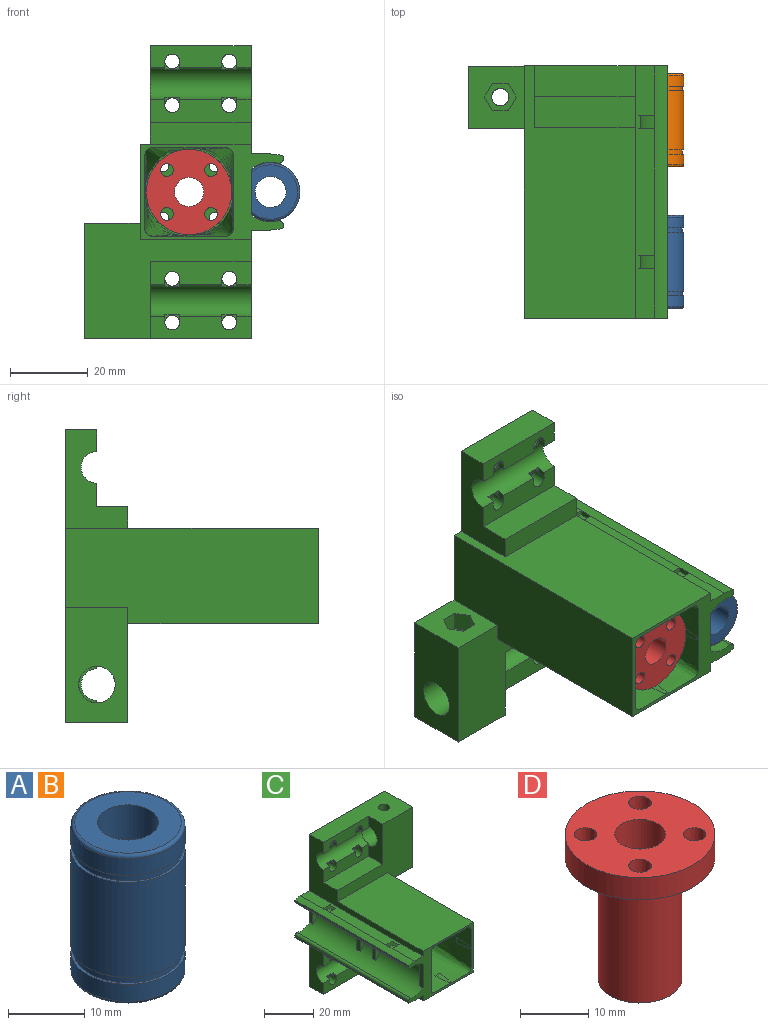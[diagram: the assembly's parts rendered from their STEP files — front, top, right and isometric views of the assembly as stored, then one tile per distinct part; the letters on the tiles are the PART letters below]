
ASSEMBLY  parts=4 mates=1
PART A: 14 faces, bbox 16.2x16.2x24 mm
  f0: plane 15x15mm, normal (0,0,-1), area 16.1mm2, adj f1,f10
  f1: cylinder r=7.15mm len=14.3mm, axis (0,0,-1), area 49.4mm2, adj f0,f2
  f2: plane 15x15mm, normal (0,0,1), area 16.1mm2, adj f1,f3
  f3: cylinder r=7.5mm len=15mm, axis (0,0,-1), area 129.6mm2, adj f2,f12
  f4: plane 14x14mm, normal (0,0,-1), area 103.7mm2, adj f11,f12
  f5: plane 14x14mm, normal (0,0,1), area 103.7mm2, adj f11,f13
  f6: cylinder r=7.5mm len=15mm, axis (0,0,-1), area 129.6mm2, adj f7,f13
  f7: plane 15x15mm, normal (0,0,-1), area 16.1mm2, adj f6,f8
  f8: cylinder r=7.15mm len=14.3mm, axis (0,0,-1), area 49.4mm2, adj f7,f9
  f9: plane 15x15mm, normal (0,0,1), area 16.1mm2, adj f8,f10
  f10: cylinder r=7.5mm len=15.3mm, axis (0,0,-1), area 721mm2, adj f0,f9
  f11: cylinder r=4mm len=24mm, axis (0,0,1), area 603.2mm2, adj f4,f5
  f12: torus R=7mm, axis (0,0,1), area 36.1mm2, adj f3,f4
  f13: torus R=7mm, axis (0,0,-1), area 36.1mm2, adj f5,f6
PART B: same geometry as A
PART C: 212 faces, bbox 51.5x65.2x75.5 mm
  f0: cylinder r=1.58mm len=4mm, axis (0,1,0), area 39.7mm2, adj f195,f203
  f1: cylinder r=1.58mm len=4mm, axis (0,1,0), area 39.7mm2, adj f188,f203
  f2: cylinder r=1.58mm len=4mm, axis (0,1,0), area 39.7mm2, adj f181,f203
  f3: cylinder r=1.58mm len=4mm, axis (0,1,0), area 39.7mm2, adj f174,f203
  f4: cylinder r=6.44mm len=16mm, axis (0,-1,0), area 647.2mm2, adj f43,f203
  f5: plane 65x5mm, normal (0,0,1), area 299.9mm2, adj f6,f8,f12,f15,f17,f21,f27,f28
  f6: cylinder r=10.43mm len=4.14mm, axis (0,-1,0), area 17.7mm2, adj f5,f8,f12,f173
  f7: cylinder r=10.43mm len=4.14mm, axis (0,-1,0), area 17.7mm2, adj f9,f13,f30,f172
  f8: plane 7.73x6.42mm, normal (0,1,0), area 16.7mm2, adj f5,f6,f10,f148,f173
  f9: plane 7.73x6.42mm, normal (0,1,0), area 16.7mm2, adj f7,f11,f30,f149,f172
  f10: cylinder r=8.43mm len=7.73mm, axis (0,-1,0), area 34.2mm2, adj f8,f12,f148,f173
  f11: cylinder r=8.43mm len=7.73mm, axis (0,-1,0), area 34.2mm2, adj f9,f13,f149,f172
  f12: plane 7.73x6.42mm, normal (0,-1,0), area 16.7mm2, adj f5,f6,f10,f148,f173
  f13: plane 7.73x6.42mm, normal (0,-1,0), area 16.7mm2, adj f7,f11,f30,f149,f172
  f14: cylinder r=10.43mm len=4.14mm, axis (0,1,0), area 17.7mm2, adj f16,f20,f30,f171
  f15: cylinder r=10.43mm len=4.14mm, axis (0,1,0), area 17.7mm2, adj f5,f17,f21,f170
  f16: plane 7.73x6.42mm, normal (0,-1,0), area 16.7mm2, adj f14,f18,f30,f151,f171
  f17: plane 7.73x6.42mm, normal (0,-1,0), area 16.7mm2, adj f5,f15,f19,f150,f170
  f18: cylinder r=8.43mm len=7.73mm, axis (0,1,0), area 34.2mm2, adj f16,f20,f151,f171
  f19: cylinder r=8.43mm len=7.73mm, axis (0,1,0), area 34.2mm2, adj f17,f21,f150,f170
  f20: plane 7.73x6.42mm, normal (0,1,0), area 16.7mm2, adj f14,f18,f30,f151,f171
  f21: plane 7.73x6.42mm, normal (0,1,0), area 16.7mm2, adj f5,f15,f19,f150,f170
  f22: cylinder r=2.24mm len=5.52mm, axis (0,0,-1), area 73.7mm2, adj f76,f166
  f23: plane 19.8x8mm, normal (-1,0,0), area 123.7mm2, adj f32,f37,f76,f108,f109,f166
  f24: cylinder r=2.24mm len=11.03mm, axis (0,0,-1), area 151.4mm2, adj f158,f166
  f25: plane 25.32x16mm, normal (1,0,0), area 220.3mm2, adj f31,f35,f39,f43,f44,f106,f107,f169
  f26: cylinder r=7.73mm len=65mm, axis (0,1,0), area 1734mm2, adj f27,f43,f138,f139,f140,f141,f142,f143
  f27: plane 37.08x24.87mm, normal (0,-1,0), area 9.6mm2, adj f5,f26,f28,f29,f30,f40,f77,f147
  f28: cylinder r=9.79mm len=65mm, axis (0,1,0), area 216.3mm2, adj f5,f27,f43,f148,f150,f153
  f29: cylinder r=9.79mm len=65mm, axis (0,1,0), area 216.3mm2, adj f27,f30,f43,f149,f151,f152
  f30: plane 65x5mm, normal (0,0,-1), area 299.9mm2, adj f7,f9,f13,f14,f16,f20,f27,f29
  f31: plane 26x5.55mm, normal (0,-1,0), area 121.3mm2, adj f25,f39,f40,f44,f60,f68,f111,f112
  f32: plane 26x6.05mm, normal (0,-1,0), area 134.2mm2, adj f23,f33,f38,f41,f77,f109,f125,f126
  f33: cylinder r=1.9mm len=4.1mm, axis (0,1,0), area 37.6mm2, adj f32,f84,f130,f131,f133
  f34: cylinder r=1.9mm len=4.1mm, axis (0,1,0), area 37mm2, adj f37,f98,f127,f128,f129
  f35: plane 26x6.05mm, normal (0,-1,0), area 134.2mm2, adj f25,f36,f39,f40,f52,f107,f114,f115
  f36: cylinder r=1.9mm len=4.1mm, axis (0,1,0), area 37mm2, adj f35,f51,f121,f122,f123
  f37: plane 26x5.55mm, normal (0,-1,0), area 121.3mm2, adj f23,f34,f38,f42,f76,f77,f128,f129
  f38: cylinder r=4.1mm len=26mm, axis (-1,0,0), area 303.2mm2, adj f32,f37,f77,f124,f125,f126,f127,f128
  f39: cylinder r=4.1mm len=26mm, axis (-1,0,0), area 303.2mm2, adj f25,f31,f35,f40,f110,f111,f112,f114
  f40: plane 65x27.86mm, normal (-1,0,0), area 385.2mm2, adj f27,f30,f31,f35,f39,f43,f44,f106
  f41: cylinder r=1.9mm len=4.1mm, axis (0,1,0), area 37mm2, adj f32,f91,f124,f125,f126
  f42: cylinder r=1.9mm len=4.1mm, axis (0,1,0), area 37.6mm2, adj f37,f105,f134,f136,f137
  f43: plane 75.3x51.25mm, normal (0,1,0), area 2052.3mm2, adj f4,f5,f25,f26,f28,f29,f30,f40
  f44: plane 26x8mm, normal (0,0,-1), area 208mm2, adj f25,f31,f40,f43
  f45: plane 3.9x3.08mm, normal (-0.87,0,0.5), area 13.9mm2, adj f43,f46,f50,f51
  f46: plane 3.9x3.08mm, normal (-0.87,0,-0.5), area 13.9mm2, adj f43,f45,f47,f51
  f47: plane 3.9x3.56mm, normal (0,0,-1), area 13.9mm2, adj f43,f46,f48,f51
  f48: plane 3.9x3.08mm, normal (0.87,0,-0.5), area 13.9mm2, adj f43,f47,f49,f51
  f49: plane 3.9x3.08mm, normal (0.87,0,0.5), area 13.9mm2, adj f43,f48,f50,f51
  f50: plane 3.9x3.56mm, normal (0,0,1), area 13.9mm2, adj f43,f45,f49,f51
  f51: plane 7.11x6.16mm, normal (0,1,0), area 21.6mm2, adj f36,f45,f46,f47,f48,f49,f50
  f52: cylinder r=1.9mm len=4.1mm, axis (0,1,0), area 37.6mm2, adj f35,f59,f115,f116,f117
  f53: plane 3.9x3.08mm, normal (-0.87,0,0.5), area 13.9mm2, adj f43,f54,f58,f59
  f54: plane 3.9x3.08mm, normal (-0.87,0,-0.5), area 13.9mm2, adj f43,f53,f55,f59
  f55: plane 3.9x3.56mm, normal (0,0,-1), area 13.9mm2, adj f43,f54,f56,f59
  f56: plane 3.9x3.08mm, normal (0.87,0,-0.5), area 13.9mm2, adj f43,f55,f57,f59
  f57: plane 3.9x3.08mm, normal (0.87,0,0.5), area 13.9mm2, adj f43,f56,f58,f59
  f58: plane 3.9x3.56mm, normal (0,0,1), area 13.9mm2, adj f43,f53,f57,f59
  f59: plane 7.11x6.16mm, normal (0,1,0), area 21.6mm2, adj f52,f53,f54,f55,f56,f57,f58
  f60: cylinder r=1.9mm len=4.1mm, axis (0,1,0), area 37mm2, adj f31,f67,f118,f119,f120
  f61: plane 3.9x3.08mm, normal (-0.87,0,0.5), area 13.9mm2, adj f43,f62,f66,f67
  f62: plane 3.9x3.08mm, normal (-0.87,0,-0.5), area 13.9mm2, adj f43,f61,f63,f67
  f63: plane 3.9x3.56mm, normal (0,0,-1), area 13.9mm2, adj f43,f62,f64,f67
  f64: plane 3.9x3.08mm, normal (0.87,0,-0.5), area 13.9mm2, adj f43,f63,f65,f67
  f65: plane 3.9x3.08mm, normal (0.87,0,0.5), area 13.9mm2, adj f43,f64,f66,f67
  f66: plane 3.9x3.56mm, normal (0,0,1), area 13.9mm2, adj f43,f61,f65,f67
  f67: plane 7.11x6.16mm, normal (0,1,0), area 21.6mm2, adj f60,f61,f62,f63,f64,f65,f66
  f68: cylinder r=1.9mm len=4.1mm, axis (0,1,0), area 37.6mm2, adj f31,f75,f110,f111,f113
  f69: plane 3.9x3.08mm, normal (-0.87,0,0.5), area 13.9mm2, adj f43,f70,f74,f75
  f70: plane 3.9x3.08mm, normal (-0.87,0,-0.5), area 13.9mm2, adj f43,f69,f71,f75
  f71: plane 3.9x3.56mm, normal (0,0,-1), area 13.9mm2, adj f43,f70,f72,f75
  f72: plane 3.9x3.08mm, normal (0.87,0,-0.5), area 13.9mm2, adj f43,f71,f73,f75
  f73: plane 3.9x3.08mm, normal (0.87,0,0.5), area 13.9mm2, adj f43,f72,f74,f75
  f74: plane 3.9x3.56mm, normal (0,0,1), area 13.9mm2, adj f43,f69,f73,f75
  f75: plane 7.11x6.16mm, normal (0,1,0), area 21.6mm2, adj f68,f69,f70,f71,f72,f73,f74
  f76: plane 42.99x16mm, normal (0,0,1), area 464mm2, adj f22,f23,f37,f43,f77,f108,f157
  f77: plane 65x27.86mm, normal (-1,0,0), area 385.2mm2, adj f5,f27,f32,f37,f38,f43,f76,f108
  f78: plane 3.9x3.08mm, normal (-0.87,0,0.5), area 13.9mm2, adj f43,f79,f83,f84
  f79: plane 3.9x3.08mm, normal (-0.87,0,-0.5), area 13.9mm2, adj f43,f78,f80,f84
  f80: plane 3.9x3.56mm, normal (0,0,-1), area 13.9mm2, adj f43,f79,f81,f84
  f81: plane 3.9x3.08mm, normal (0.87,0,-0.5), area 13.9mm2, adj f43,f80,f82,f84
  f82: plane 3.9x3.08mm, normal (0.87,0,0.5), area 13.9mm2, adj f43,f81,f83,f84
  f83: plane 3.9x3.56mm, normal (0,0,1), area 13.9mm2, adj f43,f78,f82,f84
  f84: plane 7.11x6.16mm, normal (0,1,0), area 21.6mm2, adj f33,f78,f79,f80,f81,f82,f83
  f85: plane 3.9x3.08mm, normal (-0.87,0,0.5), area 13.9mm2, adj f43,f86,f90,f91
  f86: plane 3.9x3.08mm, normal (-0.87,0,-0.5), area 13.9mm2, adj f43,f85,f87,f91
  f87: plane 3.9x3.56mm, normal (0,0,-1), area 13.9mm2, adj f43,f86,f88,f91
  f88: plane 3.9x3.08mm, normal (0.87,0,-0.5), area 13.9mm2, adj f43,f87,f89,f91
  f89: plane 3.9x3.08mm, normal (0.87,0,0.5), area 13.9mm2, adj f43,f88,f90,f91
  f90: plane 3.9x3.56mm, normal (0,0,1), area 13.9mm2, adj f43,f85,f89,f91
  f91: plane 7.11x6.16mm, normal (0,1,0), area 21.6mm2, adj f41,f85,f86,f87,f88,f89,f90
  f92: plane 3.9x3.08mm, normal (-0.87,0,0.5), area 13.9mm2, adj f43,f93,f97,f98
  f93: plane 3.9x3.08mm, normal (-0.87,0,-0.5), area 13.9mm2, adj f43,f92,f94,f98
  f94: plane 3.9x3.56mm, normal (0,0,-1), area 13.9mm2, adj f43,f93,f95,f98
  f95: plane 3.9x3.08mm, normal (0.87,0,-0.5), area 13.9mm2, adj f43,f94,f96,f98
  f96: plane 3.9x3.08mm, normal (0.87,0,0.5), area 13.9mm2, adj f43,f95,f97,f98
  f97: plane 3.9x3.56mm, normal (0,0,1), area 13.9mm2, adj f43,f92,f96,f98
  f98: plane 7.11x6.16mm, normal (0,1,0), area 21.6mm2, adj f34,f92,f93,f94,f95,f96,f97
  f99: plane 3.9x3.08mm, normal (-0.87,0,0.5), area 13.9mm2, adj f43,f100,f104,f105
  f100: plane 3.9x3.08mm, normal (-0.87,0,-0.5), area 13.9mm2, adj f43,f99,f101,f105
  f101: plane 3.9x3.56mm, normal (0,0,-1), area 13.9mm2, adj f43,f100,f102,f105
  f102: plane 3.9x3.08mm, normal (0.87,0,-0.5), area 13.9mm2, adj f43,f101,f103,f105
  f103: plane 3.9x3.08mm, normal (0.87,0,0.5), area 13.9mm2, adj f43,f102,f104,f105
  f104: plane 3.9x3.56mm, normal (0,0,1), area 13.9mm2, adj f43,f99,f103,f105
  f105: plane 7.11x6.16mm, normal (0,1,0), area 21.6mm2, adj f42,f99,f100,f101,f102,f103,f104
  f106: plane 26x5.52mm, normal (0,-1,0), area 143.5mm2, adj f25,f40,f107,f169
  f107: plane 26x8mm, normal (0,0,-1), area 208mm2, adj f25,f35,f40,f106
  f108: plane 42.99x29.66mm, normal (0,-1,0), area 636.2mm2, adj f23,f76,f77,f109,f156,f157,f167,f168
  f109: plane 26x8mm, normal (0,0,1), area 208mm2, adj f23,f32,f77,f108
  f110: plane 3.8x2.07mm, normal (0,-1,0), area 2.2mm2, adj f39,f68,f111,f112,f113
  f111: plane 2x1.77mm, normal (1,0,0), area 2.8mm2, adj f31,f39,f68,f110
  f112: plane 2.07x2mm, normal (-1,0,0), area 3.4mm2, adj f31,f39,f110,f113
  f113: plane 2x0.02mm, normal (0,0,1), area 0mm2, adj f31,f68,f110,f112
  f114: plane 2.08x2mm, normal (-1,0,0), area 3.4mm2, adj f35,f39,f116,f117
  f115: plane 2x1.78mm, normal (1,0,0), area 2.9mm2, adj f35,f39,f52,f116
  f116: plane 3.8x2.08mm, normal (0,-1,0), area 2.2mm2, adj f39,f52,f114,f115,f117
  f117: plane 2x0.02mm, normal (0,0,-1), area 0mm2, adj f35,f52,f114,f116
  f118: plane 3.8x2.07mm, normal (0,-1,0), area 2.2mm2, adj f39,f60,f119,f120
  f119: plane 2.07x2mm, normal (-1,0,0), area 3.4mm2, adj f31,f39,f60,f118
  f120: plane 2.07x2mm, normal (1,0,0), area 3.4mm2, adj f31,f39,f60,f118
  f121: plane 2.08x2mm, normal (1,0,0), area 3.4mm2, adj f35,f36,f39,f123
  f122: plane 2.08x2mm, normal (-1,0,0), area 3.4mm2, adj f35,f36,f39,f123
  f123: plane 3.8x2.08mm, normal (0,-1,0), area 2.2mm2, adj f36,f39,f121,f122
  f124: plane 3.8x2.08mm, normal (0,-1,0), area 2.2mm2, adj f38,f41,f125,f126
  f125: plane 2.08x2mm, normal (-1,0,0), area 3.4mm2, adj f32,f38,f41,f124
  f126: plane 2.08x2mm, normal (1,0,0), area 3.4mm2, adj f32,f38,f41,f124
  f127: plane 3.8x2.07mm, normal (0,-1,0), area 2.2mm2, adj f34,f38,f128,f129
  f128: plane 2.07x2mm, normal (1,0,0), area 3.4mm2, adj f34,f37,f38,f127
  f129: plane 2.07x2mm, normal (-1,0,0), area 3.4mm2, adj f34,f37,f38,f127
  f130: plane 3.8x2.08mm, normal (0,-1,0), area 2.2mm2, adj f33,f38,f131,f132,f133
  f131: plane 2x1.78mm, normal (1,0,0), area 2.9mm2, adj f32,f33,f38,f130
  f132: plane 2.08x2mm, normal (-1,0,0), area 3.4mm2, adj f32,f38,f130,f133
  f133: plane 2x0.02mm, normal (0,0,1), area 0mm2, adj f32,f33,f130,f132
  f134: plane 3.8x2.07mm, normal (0,-1,0), area 2.2mm2, adj f38,f42,f135,f136,f137
  f135: plane 2.07x2mm, normal (-1,0,0), area 3.4mm2, adj f37,f38,f134,f136
  f136: plane 2x0.02mm, normal (0,0,-1), area 0mm2, adj f37,f42,f134,f135
  f137: plane 2x1.77mm, normal (1,0,0), area 2.8mm2, adj f37,f38,f42,f134
  f138: plane 11.78x2.73mm, normal (0,-1,0), area 22.3mm2, adj f26,f139
  f139: plane 11.78x2mm, normal (-1,0,0), area 23.6mm2, adj f26,f43,f138
  f140: plane 11.78x2.73mm, normal (0,-1,0), area 22.3mm2, adj f26,f142
  f141: plane 11.78x2.73mm, normal (0,1,0), area 22.3mm2, adj f26,f142
  f142: plane 11.78x2mm, normal (-1,0,0), area 23.6mm2, adj f26,f140,f141
  f143: plane 11.78x2.73mm, normal (0,1,0), area 22.3mm2, adj f26,f145
  f144: plane 11.78x2.73mm, normal (0,-1,0), area 22.3mm2, adj f26,f145
  f145: plane 11.78x2mm, normal (-1,0,0), area 23.6mm2, adj f26,f143,f144
  f146: plane 11.78x2.73mm, normal (0,1,0), area 22.3mm2, adj f26,f147
  f147: plane 11.78x2mm, normal (-1,0,0), area 23.6mm2, adj f26,f27,f146
  f148: plane 3.5x1.37mm, normal (1,0,0), area 4.8mm2, adj f8,f10,f12,f28
  f149: plane 3.5x1.37mm, normal (1,0,0), area 4.8mm2, adj f9,f11,f13,f29
  f150: plane 3.5x1.37mm, normal (1,0,0), area 4.8mm2, adj f17,f19,f21,f28
  f151: plane 3.5x1.37mm, normal (1,0,0), area 4.8mm2, adj f16,f18,f20,f29
  f152: plane 65x0.81mm, normal (-1,0,0), area 52.5mm2, adj f27,f29,f43,f155
  f153: plane 65x0.81mm, normal (-1,0,0), area 52.5mm2, adj f27,f28,f43,f154
  f154: cylinder r=1mm len=65mm, axis (0,1,0), area 119.2mm2, adj f26,f27,f43,f153
  f155: cylinder r=1mm len=65mm, axis (0,1,0), area 119.2mm2, adj f26,f27,f43,f152
  f156: plane 16x14.39mm, normal (0,0,-1), area 186.1mm2, adj f43,f108,f157,f159,f160,f161,f162,f163
  f157: plane 29.66x16mm, normal (1,0,0), area 405.2mm2, adj f43,f76,f108,f156,f166
  f158: plane 8.24x7.14mm, normal (0,0,-1), area 28.3mm2, adj f24,f159,f160,f161,f162,f163,f164
  f159: plane 4.85x3.57mm, normal (-0.87,-0.5,0), area 20mm2, adj f156,f158,f160,f164
  f160: plane 4.85x3.57mm, normal (-0.87,0.5,0), area 20mm2, adj f156,f158,f159,f161
  f161: plane 4.85x4.12mm, normal (0,1,0), area 20mm2, adj f156,f158,f160,f162
  f162: plane 4.85x3.57mm, normal (0.87,0.5,0), area 20mm2, adj f156,f158,f161,f163
  f163: plane 4.85x3.57mm, normal (0.87,-0.5,0), area 20mm2, adj f156,f158,f162,f164
  f164: plane 4.85x4.12mm, normal (0,-1,0), area 20mm2, adj f156,f158,f159,f163
  f165: plane 9.4x4.7mm, normal (1,0,0), area 8.3mm2, adj f32,f37,f38,f166
  f166: cylinder r=4.7mm len=16.99mm, axis (1,0,0), area 469.1mm2, adj f22,f23,f24,f157,f165
  f167: plane 65x24.66mm, normal (1,0,0), area 1533.5mm2, adj f27,f43,f108,f156,f168,f169
  f168: plane 49x28.6mm, normal (0,0,1), area 1401.4mm2, adj f27,f77,f108,f167
  f169: plane 65x28.6mm, normal (0,0,-1), area 1443mm2, adj f25,f27,f40,f43,f106,f167
  f170: plane 3.64x3.5mm, normal (-1,0,0), area 12.7mm2, adj f15,f17,f19,f21
  f171: plane 3.64x3.5mm, normal (-1,0,0), area 12.7mm2, adj f14,f16,f18,f20
  f172: plane 3.64x3.5mm, normal (-1,0,0), area 12.7mm2, adj f7,f9,f11,f13
  f173: plane 3.64x3.5mm, normal (-1,0,0), area 12.7mm2, adj f6,f8,f10,f12
  f174: plane 6.47x5.6mm, normal (0,1,0), area 19.3mm2, adj f3,f175,f176,f177,f178,f179,f180
  f175: plane 12x2.8mm, normal (0.87,0,0.5), area 38.8mm2, adj f43,f174,f176,f180
  f176: plane 12x2.8mm, normal (0.87,0,-0.5), area 38.8mm2, adj f43,f174,f175,f177
  f177: plane 12x3.23mm, normal (0,0,-1), area 38.8mm2, adj f43,f174,f176,f178
  f178: plane 12x2.8mm, normal (-0.87,0,-0.5), area 38.8mm2, adj f43,f174,f177,f179
  f179: plane 12x2.8mm, normal (-0.87,0,0.5), area 38.8mm2, adj f43,f174,f178,f180
  f180: plane 12x3.23mm, normal (0,0,1), area 38.8mm2, adj f43,f174,f175,f179
  f181: plane 6.47x5.6mm, normal (0,1,0), area 19.3mm2, adj f2,f182,f183,f184,f185,f186,f187
  f182: plane 12x2.8mm, normal (0.87,0,0.5), area 38.8mm2, adj f43,f181,f183,f187
  f183: plane 12x2.8mm, normal (0.87,0,-0.5), area 38.8mm2, adj f43,f181,f182,f184
  f184: plane 12x3.23mm, normal (0,0,-1), area 38.8mm2, adj f43,f181,f183,f185
  f185: plane 12x2.8mm, normal (-0.87,0,-0.5), area 38.8mm2, adj f43,f181,f184,f186
  f186: plane 12x2.8mm, normal (-0.87,0,0.5), area 38.8mm2, adj f43,f181,f185,f187
  f187: plane 12x3.23mm, normal (0,0,1), area 38.8mm2, adj f43,f181,f182,f186
  f188: plane 6.47x5.6mm, normal (0,1,0), area 19.3mm2, adj f1,f189,f190,f191,f192,f193,f194
  f189: plane 12x2.8mm, normal (0.87,0,0.5), area 38.8mm2, adj f43,f188,f190,f194
  f190: plane 12x2.8mm, normal (0.87,0,-0.5), area 38.8mm2, adj f43,f188,f189,f191
  f191: plane 12x3.23mm, normal (0,0,-1), area 38.8mm2, adj f43,f188,f190,f192
  f192: plane 12x2.8mm, normal (-0.87,0,-0.5), area 38.8mm2, adj f43,f188,f191,f193
  f193: plane 12x2.8mm, normal (-0.87,0,0.5), area 38.8mm2, adj f43,f188,f192,f194
  f194: plane 12x3.23mm, normal (0,0,1), area 38.8mm2, adj f43,f188,f189,f193
  f195: plane 6.47x5.6mm, normal (0,1,0), area 19.3mm2, adj f0,f196,f197,f198,f199,f200,f201
  f196: plane 12x2.8mm, normal (0.87,0,0.5), area 38.8mm2, adj f43,f195,f197,f201
  f197: plane 12x2.8mm, normal (0.87,0,-0.5), area 38.8mm2, adj f43,f195,f196,f198
  f198: plane 12x3.23mm, normal (0,0,-1), area 38.8mm2, adj f43,f195,f197,f199
  f199: plane 12x2.8mm, normal (-0.87,0,-0.5), area 38.8mm2, adj f43,f195,f198,f200
  f200: plane 12x2.8mm, normal (-0.87,0,0.5), area 38.8mm2, adj f43,f195,f199,f201
  f201: plane 12x3.23mm, normal (0,0,1), area 38.8mm2, adj f43,f195,f196,f200
  f202: bspline ~49x22.87mm, area 3821.7mm2, adj f27,f203,f204,f205,f206,f207,f208,f209
  f203: plane 22.91x22.91mm, normal (0,-1,0), area 249mm2, adj f0,f1,f2,f3,f4,f202
  f204: plane 2.65x0.11mm, normal (0,-1,0), area 0.1mm2, adj f202,f205
  f205: cylinder r=11.43mm len=8.1mm, axis (0,-1,0), area 14.5mm2, adj f202,f204
  f206: plane 2.65x0.11mm, normal (0,-1,0), area 0.1mm2, adj f202,f207
  f207: cylinder r=11.43mm len=8.1mm, axis (0,-1,0), area 14.5mm2, adj f202,f206
  f208: plane 2.65x0.11mm, normal (0,-1,0), area 0.1mm2, adj f202,f209
  f209: cylinder r=11.43mm len=8.1mm, axis (0,-1,0), area 14.5mm2, adj f202,f208
  f210: plane 2.65x0.11mm, normal (0,-1,0), area 0.1mm2, adj f202,f211
  f211: cylinder r=11.43mm len=8.1mm, axis (0,-1,0), area 14.5mm2, adj f202,f210
PART D: 10 faces, bbox 22x22x26 mm
  f0: cylinder r=11mm len=22mm, axis (0,0,-1), area 276.5mm2, adj f6,f7
  f1: cylinder r=1.65mm len=4mm, axis (0,0,-1), area 41.5mm2, adj f6,f7
  f2: cylinder r=1.65mm len=4mm, axis (0,0,-1), area 41.5mm2, adj f6,f7
  f3: cylinder r=3.75mm len=25.95mm, axis (0,0,-1), area 611.4mm2, adj f6,f9
  f4: cylinder r=1.65mm len=4mm, axis (0,0,-1), area 41.5mm2, adj f6,f7
  f5: cylinder r=1.65mm len=4mm, axis (0,0,-1), area 41.5mm2, adj f6,f7
  f6: plane 22x22mm, normal (0,0,1), area 301.7mm2, adj f0,f1,f2,f3,f4,f5
  f7: plane 22x22mm, normal (0,0,-1), area 227.1mm2, adj f0,f1,f2,f4,f5,f8
  f8: cylinder r=6.15mm len=21.95mm, axis (0,0,1), area 848.2mm2, adj f7,f9
  f9: plane 12.3x12.3mm, normal (0,0,-1), area 74.6mm2, adj f3,f8
PLACE A rot(axis=(0.99,-0.09,0.09),90.5deg) t=(-18.91,-48.74,117.51)mm
PLACE B rot(axis=(-0.14,0.7,0.7),164.1deg) t=(-18.91,-36.24,117.51)mm
PLACE C rot(axis=(0,1,0),180deg) t=(-18.91,-10.24,117.51)mm
PLACE D rot(axis=(0,0.71,-0.71),180deg) t=(-39.91,-67.14,117.51)mm
MATE fastened D.f0 <-> C.f205  axis (0,1,0) through (-39.91,-67.14,117.51)mm
